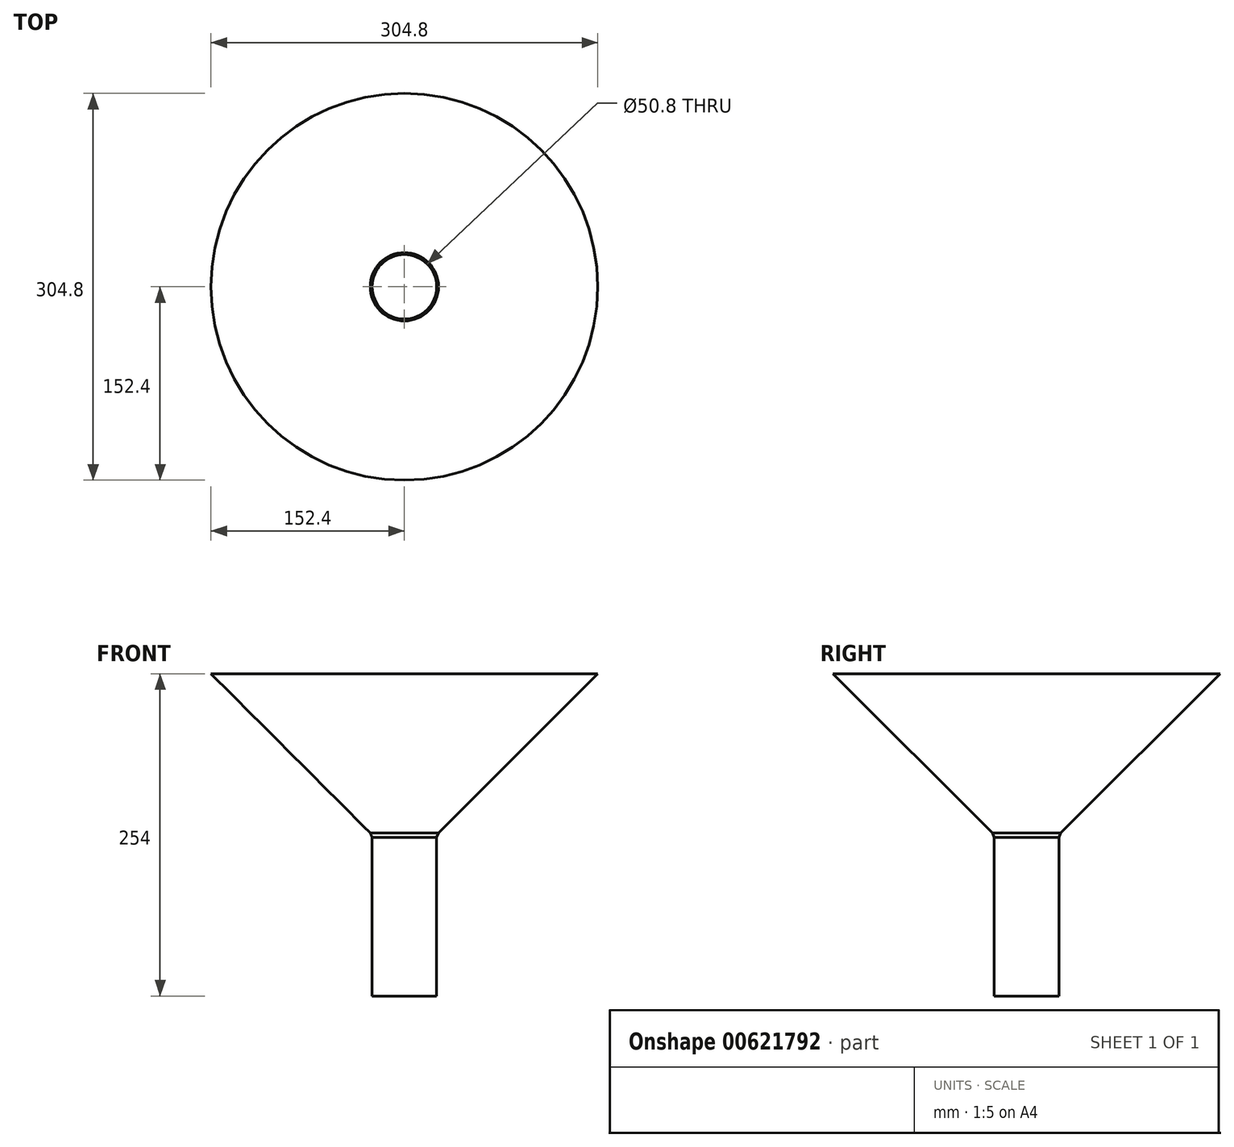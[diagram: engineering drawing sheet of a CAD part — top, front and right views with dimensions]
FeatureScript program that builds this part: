
annotation { "Feature Type Name" : "Feature", "Feature Type Description" : "" }
export const myFeature = defineFeature(function(context is Context, id is Id, definition is map)
    precondition{}
    {
        {
            var Q0;
            Q0=qCreatedBy(makeId("Front.planeOp"),FACE);
            var sketch = newSketch(context, id + "F0", { "sketchPlane" : qUnion([Q0])});
            skLineSegment(sketch, "E0.bottom", {"start": v(-25.4, -63.5) * mm, "end": v(25.4, -63.5) * mm});
            skLineSegment(sketch, "E0.left", {"start": v(-25.4, -63.5) * mm, "end": v(-25.4, 63.5) * mm});
            skLineSegment(sketch, "E0.right", {"start": v(25.4, -63.5) * mm, "end": v(25.4, 63.5) * mm});
            skPoint(sketch, "E0.middle", {"position": v(0, 0) * mm});
            skLineSegment(sketch, "E1", {"start": v(0, 252.21) * mm, "end": v(0, -63.5) * mm, "construction": true});
            skLineSegment(sketch, "E2", {"start": v(0, 190.5) * mm, "end": v(-152.4, 190.5) * mm});
            skLineSegment(sketch, "E3", {"start": v(-152.4, 190.5) * mm, "end": v(152.4, 190.5) * mm});
            skLineSegment(sketch, "E4", {"start": v(-152.4, 190.5) * mm, "end": v(-25.4, 63.5) * mm});
            skLineSegment(sketch, "E5", {"start": v(152.4, 190.5) * mm, "end": v(25.4, 63.5) * mm});
            skSolve(sketch);
        }
        {
            var Q0;
            Q0=makeQuery(id+"F0.imprint","IMPRINT",FACE,{"disambiguationData":[TD([[makeQuery(id+"F0.imprint","IMPRINT",EDGE,{"derivedFrom":sQuery(id+"F0.wireOp",EDGE,"E0.bottom")}),1.0]])]});
            var Q1;
            Q1=sQuery(id+"F0.wireOp",EDGE,"E5");
            var Q2;
            Q2=sQuery(id+"F0.wireOp",EDGE,"E0.right");
            var Q3;
            Q3=sQuery(id+"F0.wireOp",EDGE,"E1");
            revolve(context, id + "F1", {"bodyType" : ToolBodyType.SURFACE, "entities" : qUnion([Q0]), "surfaceEntities" : qUnion([Q1, Q2]), "axis" : qUnion([Q3]), "revolveType" : RevolveType.FULL});
        }
        {
            var Q0;
            Q0=makeQuery(id+"F1.opRevolve","SWEPT_FACE",FACE,{"disambiguationData":[OSD([sQuery(id+"F0.wireOp",EDGE,"E5")])]});
            var Q1;
            Q1=makeQuery(id+"F1.opRevolve","SWEPT_FACE",FACE,{"disambiguationData":[OSD([sQuery(id+"F0.wireOp",EDGE,"E0.right")])]});
            chamfer(context, id + "F2", {"entities" : qUnion([Q0, Q1]), "width" : 5.08 * mm, "tangentPropagation" : true});
        }
    });
